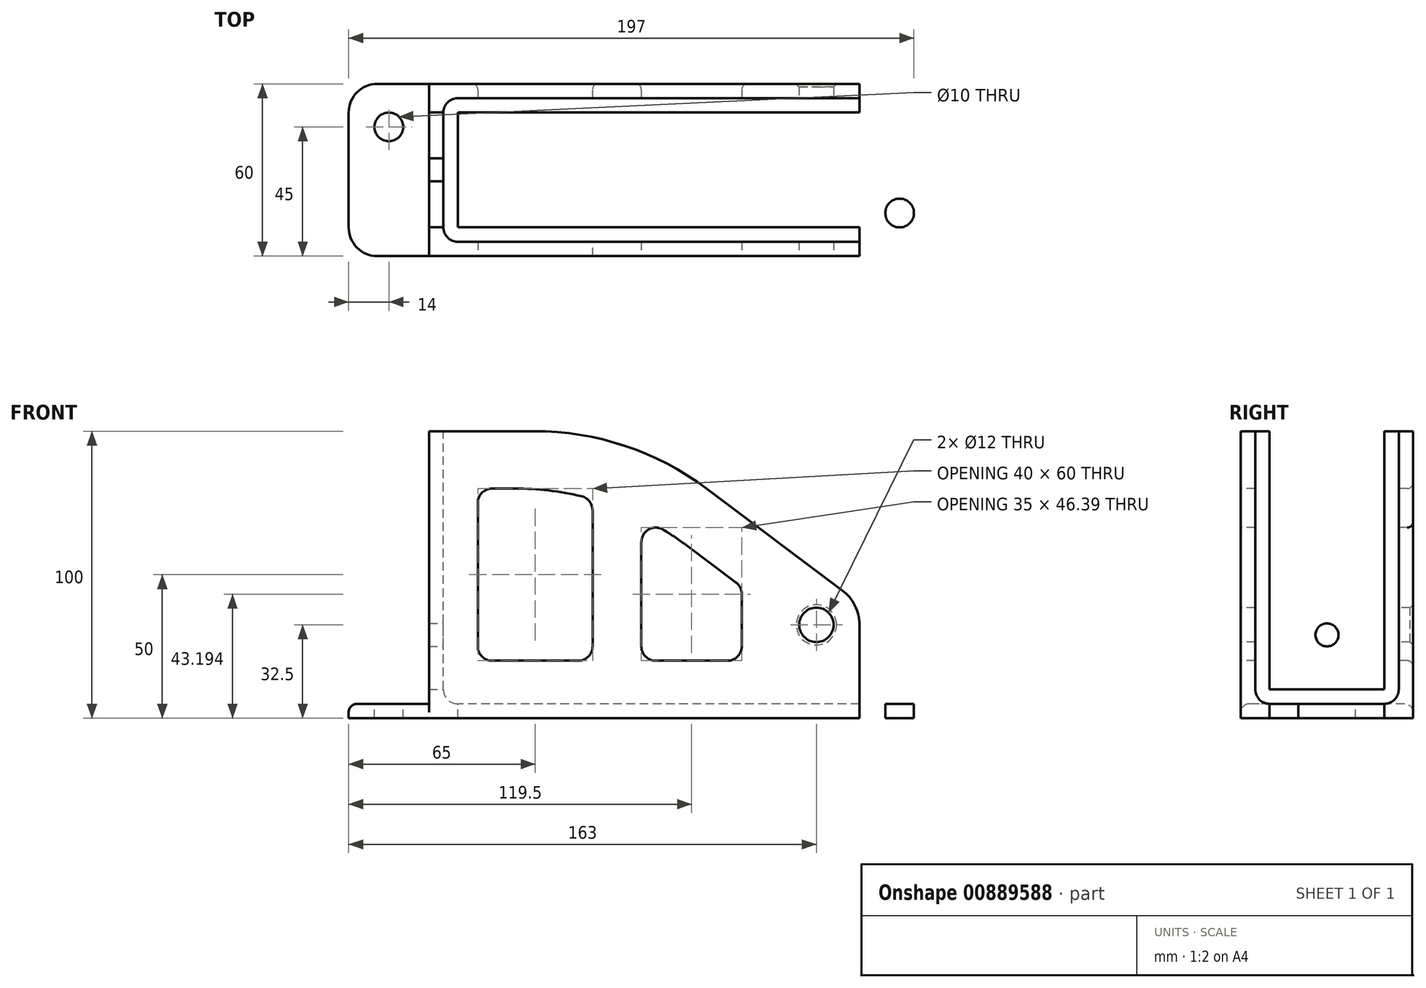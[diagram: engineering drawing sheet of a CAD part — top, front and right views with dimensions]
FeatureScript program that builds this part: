
annotation { "Feature Type Name" : "Feature", "Feature Type Description" : "" }
export const myFeature = defineFeature(function(context is Context, id is Id, definition is map)
    precondition{}
    {
        {
            var Q0;
            Q0=qCreatedBy(makeId("Front.planeOp"),FACE);
            var sketch = newSketch(context, id + "F0", { "sketchPlane" : qUnion([Q0])});
            skLineSegment(sketch, "E0", {"start": v(0, 0) * mm, "end": v(0, 100) * mm});
            skLineSegment(sketch, "E1", {"start": v(0, 100) * mm, "end": v(70, 100) * mm});
            skLineSegment(sketch, "E2", {"start": v(70, 100) * mm, "end": v(150, 40) * mm});
            skLineSegment(sketch, "E3", {"start": v(150, 40) * mm, "end": v(150, 0) * mm});
            skLineSegment(sketch, "E4", {"start": v(150, 0) * mm, "end": v(0, 0) * mm});
            skSolve(sketch);
        }
        {
            var Q0;
            Q0=makeQuery(id+"F0.imprint","IMPRINT",FACE,{"disambiguationData":[TD([[makeQuery(id+"F0.imprint","IMPRINT",EDGE,{"derivedFrom":sQuery(id+"F0.wireOp",EDGE,"E0")}),-1.0]])]});
            extrude(context, id + "F1", {"entities" : qUnion([Q0]), "depth" : 60 * mm, "offsetDistance" : 25 * mm});
        }
        {
            var Q0;
            Q0=makeQuery(id+"F1.opExtrude","SWEPT_FACE",FACE,{"disambiguationData":[OSD([sQuery(id+"F0.wireOp",EDGE,"E3")])]});
            var Q1;
            Q1=makeQuery(id+"F1.opExtrude","SWEPT_FACE",FACE,{"disambiguationData":[OSD([sQuery(id+"F0.wireOp",EDGE,"E2")])]});
            var Q2;
            Q2=makeQuery(id+"F1.opExtrude","SWEPT_FACE",FACE,{"disambiguationData":[OSD([sQuery(id+"F0.wireOp",EDGE,"E1")])]});
            shell(context, id + "F2", {"entities" : qUnion([Q0, Q1, Q2]), "thickness" : 5 * mm});
        }
        {
            var Q0;
            Q0=makeQuery(id+"F1.opExtrude","SWEPT_EDGE",EDGE,{"disambiguationData":[OSD([sQuery(id+"F0.wireOp",EDGE,"E1"),sQuery(id+"F0.wireOp",EDGE,"E2")])]});
            var Q1;
            Q1=makeQuery(id+"F2.opShell","OFFSET_EDGE",EDGE,{"disambiguationData":[OSD([sQuery(id+"F0.wireOp",EDGE,"E1"),sQuery(id+"F0.wireOp",EDGE,"E2")])]});
            fillet(context, id + "F3", {"entities" : qUnion([Q0, Q1]), "radius" : 100 * mm, "tangentPropagation" : true, "allowEdgeOverflow" : false});
        }
        {
            var Q0;
            Q0=makeQuery(id+"F1.opExtrude","SWEPT_EDGE",EDGE,{"disambiguationData":[OSD([sQuery(id+"F0.wireOp",EDGE,"E2"),sQuery(id+"F0.wireOp",EDGE,"E3")])]});
            var Q1;
            Q1=makeQuery(id+"F2.opShell","OFFSET_EDGE",EDGE,{"disambiguationData":[OSD([sQuery(id+"F0.wireOp",EDGE,"E2"),sQuery(id+"F0.wireOp",EDGE,"E3")])]});
            fillet(context, id + "F4", {"entities" : qUnion([Q0, Q1]), "radius" : 15 * mm, "tangentPropagation" : true, "allowEdgeOverflow" : false});
        }
        {
            var Q0;
            Q0=makeQuery(id+"F1.opExtrude","CAP_FACE",FACE,{"disambiguationData":[OSD([sQuery(id+"F0.wireOp",EDGE,"E0"),sQuery(id+"F0.wireOp",EDGE,"E1"),sQuery(id+"F0.wireOp",EDGE,"E2"),sQuery(id+"F0.wireOp",EDGE,"E3"),sQuery(id+"F0.wireOp",EDGE,"E4")])],"isStart":false});
            var sketch = newSketch(context, id + "F5", { "sketchPlane" : qUnion([Q0])});
            skLineSegment(sketch, "E5", {"start": v(17, 80) * mm, "end": v(30, 80) * mm});
            skLineSegment(sketch, "E6", {"start": v(90, 60) * mm, "end": v(109, 45.75) * mm});
            skLineSegment(sketch, "E7", {"start": v(109, 45.75) * mm, "end": v(109, 20) * mm});
            skLineSegment(sketch, "E8", {"start": v(109, 20) * mm, "end": v(74, 20) * mm});
            skLineSegment(sketch, "E9", {"start": v(17, 20) * mm, "end": v(17, 80) * mm});
            skPoint(sketch, "E10.visualSharp", {"position": v(63.33, 80) * mm});
            skArc(sketch, "E10.filletArc", {"start": v(90, 60) * mm, "mid": v(82.23, 65.28) * mm, "end": v(74, 69.8) * mm});
            skLineSegment(sketch, "E11", {"start": v(57, 20) * mm, "end": v(57, 76.29) * mm});
            skLineSegment(sketch, "E12", {"start": v(74, 20) * mm, "end": v(74, 69.8) * mm});
            skArc(sketch, "E13.trimOffspring", {"start": v(57, 76.29) * mm, "mid": v(43.63, 79.07) * mm, "end": v(30, 80) * mm});
            skLineSegment(sketch, "E14.trimOffspring", {"start": v(57, 20) * mm, "end": v(17, 20) * mm});
            skSolve(sketch);
        }
        {
            var Q0;
            Q0=makeQuery(id+"F5.imprint","IMPRINT",FACE,{"disambiguationData":[TD([[makeQuery(id+"F5.imprint","IMPRINT",EDGE,{"derivedFrom":sQuery(id+"F5.wireOp",EDGE,"E5")}),-1.0]])]});
            var Q1;
            Q1=makeQuery(id+"F5.imprint","IMPRINT",FACE,{"disambiguationData":[TD([[makeQuery(id+"F5.imprint","IMPRINT",EDGE,{"derivedFrom":sQuery(id+"F5.wireOp",EDGE,"E6")}),-1.0]])]});
            extrude(context, id + "F6", {"entities" : qUnion([Q0, Q1]), "operationType" : NewBodyOperationType.REMOVE, "endBound" : BoundingType.THROUGH_ALL, "oppositeDirection" : true, "depth" : 25 * mm, "offsetDistance" : 25 * mm});
        }
        {
            var Q0;
            {var subQ0=sQuery(id+"F0.wireOp",EDGE,"E4");var subQ1=sQuery(id+"F0.wireOp",EDGE,"E3");var subQ2=sQuery(id+"F0.wireOp",EDGE,"E2");var subQ3=sQuery(id+"F0.wireOp",EDGE,"E1");var subQ4=sQuery(id+"F0.wireOp",EDGE,"E0");var subQ5=makeQuery(id+"F1.opExtrude","CAP_FACE",FACE,{"disambiguationData":[OSD([subQ4,subQ3,subQ2,subQ1,subQ0])],"isStart":false});var subQ6=sQuery(id+"F5.wireOp",EDGE,"E9");var subQ7=sQuery(id+"F5.wireOp",EDGE,"E14.trimOffspring");Q0=makeQuery(id+"F6.boolean.opBoolean","COPY",EDGE,{"disambiguationData":[TD([subQ5])],"derivedFrom":makeQuery(id+"F6.opExtrude","SWEPT_EDGE",EDGE,{"disambiguationData":[OSD([subQ6,subQ7])]})});}
            var Q1;
            {var subQ0=sQuery(id+"F0.wireOp",EDGE,"E4");var subQ1=sQuery(id+"F0.wireOp",EDGE,"E3");var subQ2=sQuery(id+"F0.wireOp",EDGE,"E2");var subQ3=sQuery(id+"F0.wireOp",EDGE,"E1");var subQ4=sQuery(id+"F0.wireOp",EDGE,"E0");var subQ5=makeQuery(id+"F1.opExtrude","CAP_FACE",FACE,{"disambiguationData":[OSD([subQ4,subQ3,subQ2,subQ1,subQ0])],"isStart":false});var subQ6=sQuery(id+"F5.wireOp",EDGE,"E11");var subQ7=sQuery(id+"F5.wireOp",EDGE,"E14.trimOffspring");Q1=makeQuery(id+"F6.boolean.opBoolean","COPY",EDGE,{"disambiguationData":[TD([subQ5])],"derivedFrom":makeQuery(id+"F6.opExtrude","SWEPT_EDGE",EDGE,{"disambiguationData":[OSD([subQ6,subQ7])]})});}
            var Q2;
            {var subQ0=sQuery(id+"F0.wireOp",EDGE,"E4");var subQ1=sQuery(id+"F0.wireOp",EDGE,"E3");var subQ2=sQuery(id+"F0.wireOp",EDGE,"E2");var subQ3=sQuery(id+"F0.wireOp",EDGE,"E1");var subQ4=sQuery(id+"F0.wireOp",EDGE,"E0");var subQ5=makeQuery(id+"F1.opExtrude","CAP_FACE",FACE,{"disambiguationData":[OSD([subQ4,subQ3,subQ2,subQ1,subQ0])],"isStart":false});var subQ6=sQuery(id+"F5.wireOp",EDGE,"E12");var subQ7=sQuery(id+"F5.wireOp",EDGE,"E8");Q2=makeQuery(id+"F6.boolean.opBoolean","COPY",EDGE,{"disambiguationData":[TD([subQ5])],"derivedFrom":makeQuery(id+"F6.opExtrude","SWEPT_EDGE",EDGE,{"disambiguationData":[OSD([subQ7,subQ6])]})});}
            var Q3;
            {var subQ0=sQuery(id+"F0.wireOp",EDGE,"E4");var subQ1=sQuery(id+"F0.wireOp",EDGE,"E3");var subQ2=sQuery(id+"F0.wireOp",EDGE,"E2");var subQ3=sQuery(id+"F0.wireOp",EDGE,"E1");var subQ4=sQuery(id+"F0.wireOp",EDGE,"E0");var subQ5=makeQuery(id+"F1.opExtrude","CAP_FACE",FACE,{"disambiguationData":[OSD([subQ4,subQ3,subQ2,subQ1,subQ0])],"isStart":false});var subQ6=sQuery(id+"F5.wireOp",EDGE,"E7");var subQ7=sQuery(id+"F5.wireOp",EDGE,"E8");Q3=makeQuery(id+"F6.boolean.opBoolean","COPY",EDGE,{"disambiguationData":[TD([subQ5])],"derivedFrom":makeQuery(id+"F6.opExtrude","SWEPT_EDGE",EDGE,{"disambiguationData":[OSD([subQ6,subQ7])]})});}
            var Q4;
            {var subQ0=sQuery(id+"F0.wireOp",EDGE,"E4");var subQ1=sQuery(id+"F0.wireOp",EDGE,"E3");var subQ2=sQuery(id+"F0.wireOp",EDGE,"E2");var subQ3=sQuery(id+"F0.wireOp",EDGE,"E1");var subQ4=sQuery(id+"F0.wireOp",EDGE,"E0");var subQ5=makeQuery(id+"F1.opExtrude","CAP_FACE",FACE,{"disambiguationData":[OSD([subQ4,subQ3,subQ2,subQ1,subQ0])],"isStart":false});var subQ6=sQuery(id+"F5.wireOp",EDGE,"E5");var subQ7=sQuery(id+"F5.wireOp",EDGE,"E9");Q4=makeQuery(id+"F6.boolean.opBoolean","COPY",EDGE,{"disambiguationData":[TD([subQ5])],"derivedFrom":makeQuery(id+"F6.opExtrude","SWEPT_EDGE",EDGE,{"disambiguationData":[OSD([subQ6,subQ7])]})});}
            var Q5;
            {var subQ0=sQuery(id+"F0.wireOp",EDGE,"E4");var subQ1=sQuery(id+"F0.wireOp",EDGE,"E3");var subQ2=sQuery(id+"F0.wireOp",EDGE,"E2");var subQ3=sQuery(id+"F0.wireOp",EDGE,"E1");var subQ4=sQuery(id+"F0.wireOp",EDGE,"E0");var subQ5=makeQuery(id+"F1.opExtrude","CAP_FACE",FACE,{"disambiguationData":[OSD([subQ4,subQ3,subQ2,subQ1,subQ0])],"isStart":false});var subQ6=sQuery(id+"F5.wireOp",EDGE,"E7");var subQ7=sQuery(id+"F5.wireOp",EDGE,"E6");Q5=makeQuery(id+"F6.boolean.opBoolean","COPY",EDGE,{"disambiguationData":[TD([subQ5])],"derivedFrom":makeQuery(id+"F6.opExtrude","SWEPT_EDGE",EDGE,{"disambiguationData":[OSD([subQ7,subQ6])]})});}
            var Q6;
            {var subQ0=sQuery(id+"F0.wireOp",EDGE,"E4");var subQ1=sQuery(id+"F0.wireOp",EDGE,"E3");var subQ2=sQuery(id+"F0.wireOp",EDGE,"E2");var subQ3=sQuery(id+"F0.wireOp",EDGE,"E1");var subQ4=sQuery(id+"F0.wireOp",EDGE,"E0");var subQ5=makeQuery(id+"F1.opExtrude","CAP_FACE",FACE,{"disambiguationData":[OSD([subQ4,subQ3,subQ2,subQ1,subQ0])],"isStart":false});var subQ6=sQuery(id+"F5.wireOp",EDGE,"E13.trimOffspring");var subQ7=sQuery(id+"F5.wireOp",EDGE,"E11");Q6=makeQuery(id+"F6.boolean.opBoolean","COPY",EDGE,{"disambiguationData":[TD([subQ5])],"derivedFrom":makeQuery(id+"F6.opExtrude","SWEPT_EDGE",EDGE,{"disambiguationData":[OSD([subQ7,subQ6])]})});}
            var Q7;
            {var subQ0=sQuery(id+"F0.wireOp",EDGE,"E4");var subQ1=sQuery(id+"F0.wireOp",EDGE,"E3");var subQ2=sQuery(id+"F0.wireOp",EDGE,"E2");var subQ3=sQuery(id+"F0.wireOp",EDGE,"E1");var subQ4=sQuery(id+"F0.wireOp",EDGE,"E0");var subQ5=makeQuery(id+"F1.opExtrude","CAP_FACE",FACE,{"disambiguationData":[OSD([subQ4,subQ3,subQ2,subQ1,subQ0])],"isStart":false});var subQ6=sQuery(id+"F5.wireOp",EDGE,"E12");var subQ7=sQuery(id+"F5.wireOp",EDGE,"E10.filletArc");Q7=makeQuery(id+"F6.boolean.opBoolean","COPY",EDGE,{"disambiguationData":[TD([subQ5])],"derivedFrom":makeQuery(id+"F6.opExtrude","SWEPT_EDGE",EDGE,{"disambiguationData":[OSD([subQ7,subQ6])]})});}
            var Q8;
            {var subQ0=sQuery(id+"F0.wireOp",EDGE,"E4");var subQ1=sQuery(id+"F0.wireOp",EDGE,"E3");var subQ2=sQuery(id+"F0.wireOp",EDGE,"E2");var subQ3=sQuery(id+"F0.wireOp",EDGE,"E1");var subQ4=sQuery(id+"F0.wireOp",EDGE,"E0");var subQ5=makeQuery(id+"F1.opExtrude","CAP_FACE",FACE,{"disambiguationData":[OSD([subQ4,subQ3,subQ2,subQ1,subQ0])],"isStart":true});var subQ6=sQuery(id+"F5.wireOp",EDGE,"E7");var subQ7=sQuery(id+"F5.wireOp",EDGE,"E8");Q8=makeQuery(id+"F6.boolean.opBoolean","COPY",EDGE,{"disambiguationData":[TD([subQ5])],"derivedFrom":makeQuery(id+"F6.opExtrude","SWEPT_EDGE",EDGE,{"disambiguationData":[OSD([subQ6,subQ7])]})});}
            var Q9;
            {var subQ0=sQuery(id+"F0.wireOp",EDGE,"E4");var subQ1=sQuery(id+"F0.wireOp",EDGE,"E3");var subQ2=sQuery(id+"F0.wireOp",EDGE,"E2");var subQ3=sQuery(id+"F0.wireOp",EDGE,"E1");var subQ4=sQuery(id+"F0.wireOp",EDGE,"E0");var subQ5=makeQuery(id+"F1.opExtrude","CAP_FACE",FACE,{"disambiguationData":[OSD([subQ4,subQ3,subQ2,subQ1,subQ0])],"isStart":true});var subQ6=sQuery(id+"F5.wireOp",EDGE,"E7");var subQ7=sQuery(id+"F5.wireOp",EDGE,"E6");Q9=makeQuery(id+"F6.boolean.opBoolean","COPY",EDGE,{"disambiguationData":[TD([subQ5])],"derivedFrom":makeQuery(id+"F6.opExtrude","SWEPT_EDGE",EDGE,{"disambiguationData":[OSD([subQ7,subQ6])]})});}
            var Q10;
            {var subQ0=sQuery(id+"F0.wireOp",EDGE,"E4");var subQ1=sQuery(id+"F0.wireOp",EDGE,"E3");var subQ2=sQuery(id+"F0.wireOp",EDGE,"E2");var subQ3=sQuery(id+"F0.wireOp",EDGE,"E1");var subQ4=sQuery(id+"F0.wireOp",EDGE,"E0");var subQ5=makeQuery(id+"F1.opExtrude","CAP_FACE",FACE,{"disambiguationData":[OSD([subQ4,subQ3,subQ2,subQ1,subQ0])],"isStart":true});var subQ6=sQuery(id+"F5.wireOp",EDGE,"E12");var subQ7=sQuery(id+"F5.wireOp",EDGE,"E8");Q10=makeQuery(id+"F6.boolean.opBoolean","COPY",EDGE,{"disambiguationData":[TD([subQ5])],"derivedFrom":makeQuery(id+"F6.opExtrude","SWEPT_EDGE",EDGE,{"disambiguationData":[OSD([subQ7,subQ6])]})});}
            var Q11;
            {var subQ0=sQuery(id+"F0.wireOp",EDGE,"E4");var subQ1=sQuery(id+"F0.wireOp",EDGE,"E3");var subQ2=sQuery(id+"F0.wireOp",EDGE,"E2");var subQ3=sQuery(id+"F0.wireOp",EDGE,"E1");var subQ4=sQuery(id+"F0.wireOp",EDGE,"E0");var subQ5=makeQuery(id+"F1.opExtrude","CAP_FACE",FACE,{"disambiguationData":[OSD([subQ4,subQ3,subQ2,subQ1,subQ0])],"isStart":true});var subQ6=sQuery(id+"F5.wireOp",EDGE,"E9");var subQ7=sQuery(id+"F5.wireOp",EDGE,"E14.trimOffspring");Q11=makeQuery(id+"F6.boolean.opBoolean","COPY",EDGE,{"disambiguationData":[TD([subQ5])],"derivedFrom":makeQuery(id+"F6.opExtrude","SWEPT_EDGE",EDGE,{"disambiguationData":[OSD([subQ6,subQ7])]})});}
            var Q12;
            {var subQ0=sQuery(id+"F0.wireOp",EDGE,"E4");var subQ1=sQuery(id+"F0.wireOp",EDGE,"E3");var subQ2=sQuery(id+"F0.wireOp",EDGE,"E2");var subQ3=sQuery(id+"F0.wireOp",EDGE,"E1");var subQ4=sQuery(id+"F0.wireOp",EDGE,"E0");var subQ5=makeQuery(id+"F1.opExtrude","CAP_FACE",FACE,{"disambiguationData":[OSD([subQ4,subQ3,subQ2,subQ1,subQ0])],"isStart":true});var subQ6=sQuery(id+"F5.wireOp",EDGE,"E12");var subQ7=sQuery(id+"F5.wireOp",EDGE,"E10.filletArc");Q12=makeQuery(id+"F6.boolean.opBoolean","COPY",EDGE,{"disambiguationData":[TD([subQ5])],"derivedFrom":makeQuery(id+"F6.opExtrude","SWEPT_EDGE",EDGE,{"disambiguationData":[OSD([subQ7,subQ6])]})});}
            var Q13;
            {var subQ0=sQuery(id+"F0.wireOp",EDGE,"E4");var subQ1=sQuery(id+"F0.wireOp",EDGE,"E3");var subQ2=sQuery(id+"F0.wireOp",EDGE,"E2");var subQ3=sQuery(id+"F0.wireOp",EDGE,"E1");var subQ4=sQuery(id+"F0.wireOp",EDGE,"E0");var subQ5=makeQuery(id+"F1.opExtrude","CAP_FACE",FACE,{"disambiguationData":[OSD([subQ4,subQ3,subQ2,subQ1,subQ0])],"isStart":true});var subQ6=sQuery(id+"F5.wireOp",EDGE,"E5");var subQ7=sQuery(id+"F5.wireOp",EDGE,"E9");Q13=makeQuery(id+"F6.boolean.opBoolean","COPY",EDGE,{"disambiguationData":[TD([subQ5])],"derivedFrom":makeQuery(id+"F6.opExtrude","SWEPT_EDGE",EDGE,{"disambiguationData":[OSD([subQ6,subQ7])]})});}
            var Q14;
            {var subQ0=sQuery(id+"F0.wireOp",EDGE,"E4");var subQ1=sQuery(id+"F0.wireOp",EDGE,"E3");var subQ2=sQuery(id+"F0.wireOp",EDGE,"E2");var subQ3=sQuery(id+"F0.wireOp",EDGE,"E1");var subQ4=sQuery(id+"F0.wireOp",EDGE,"E0");var subQ5=makeQuery(id+"F1.opExtrude","CAP_FACE",FACE,{"disambiguationData":[OSD([subQ4,subQ3,subQ2,subQ1,subQ0])],"isStart":true});var subQ6=sQuery(id+"F5.wireOp",EDGE,"E11");var subQ7=sQuery(id+"F5.wireOp",EDGE,"E14.trimOffspring");Q14=makeQuery(id+"F6.boolean.opBoolean","COPY",EDGE,{"disambiguationData":[TD([subQ5])],"derivedFrom":makeQuery(id+"F6.opExtrude","SWEPT_EDGE",EDGE,{"disambiguationData":[OSD([subQ6,subQ7])]})});}
            var Q15;
            {var subQ0=sQuery(id+"F0.wireOp",EDGE,"E4");var subQ1=sQuery(id+"F0.wireOp",EDGE,"E3");var subQ2=sQuery(id+"F0.wireOp",EDGE,"E2");var subQ3=sQuery(id+"F0.wireOp",EDGE,"E1");var subQ4=sQuery(id+"F0.wireOp",EDGE,"E0");var subQ5=makeQuery(id+"F1.opExtrude","CAP_FACE",FACE,{"disambiguationData":[OSD([subQ4,subQ3,subQ2,subQ1,subQ0])],"isStart":true});var subQ6=sQuery(id+"F5.wireOp",EDGE,"E11");var subQ7=sQuery(id+"F5.wireOp",EDGE,"E13.trimOffspring");Q15=makeQuery(id+"F6.boolean.opBoolean","COPY",EDGE,{"disambiguationData":[TD([subQ5])],"derivedFrom":makeQuery(id+"F6.opExtrude","SWEPT_EDGE",EDGE,{"disambiguationData":[OSD([subQ6,subQ7])]})});}
            var Q16;
            {var subQ0=sQuery(id+"F0.wireOp",EDGE,"E4");Q16=makeQuery(id+"F2.opShell","OFFSET_EDGE",EDGE,{"disambiguationData":[OSD([subQ0]),TDD([makeQuery(id+"F1.opExtrude","CAP_EDGE",EDGE,{"disambiguationData":[OSD([subQ0])],"isStart":false})])]});}
            var Q17;
            {var subQ0=sQuery(id+"F0.wireOp",EDGE,"E4");Q17=makeQuery(id+"F2.opShell","OFFSET_EDGE",EDGE,{"disambiguationData":[OSD([subQ0]),TDD([makeQuery(id+"F1.opExtrude","CAP_EDGE",EDGE,{"disambiguationData":[OSD([subQ0])],"isStart":true})])]});}
            var Q18;
            Q18=makeQuery(id+"F2.opShell","OFFSET_EDGE",EDGE,{"disambiguationData":[OSD([sQuery(id+"F0.wireOp",EDGE,"E0"),sQuery(id+"F0.wireOp",EDGE,"E4")])]});
            var Q19;
            {var subQ0=sQuery(id+"F0.wireOp",EDGE,"E0");Q19=makeQuery(id+"F2.opShell","OFFSET_EDGE",EDGE,{"disambiguationData":[OSD([subQ0]),TDD([makeQuery(id+"F1.opExtrude","CAP_EDGE",EDGE,{"disambiguationData":[OSD([subQ0])],"isStart":false})])]});}
            var Q20;
            {var subQ0=sQuery(id+"F0.wireOp",EDGE,"E0");Q20=makeQuery(id+"F2.opShell","OFFSET_EDGE",EDGE,{"disambiguationData":[OSD([subQ0]),TDD([makeQuery(id+"F1.opExtrude","CAP_EDGE",EDGE,{"disambiguationData":[OSD([subQ0])],"isStart":true})])]});}
            fillet(context, id + "F7", {"entities" : qUnion([Q0, Q1, Q2, Q3, Q4, Q5, Q6, Q7, Q8, Q9, Q10, Q11, Q12, Q13, Q14, Q15, Q16, Q17, Q18, Q19, Q20]), "radius" : 5 * mm, "tangentPropagation" : true, "allowEdgeOverflow" : false});
        }
        {
            var Q0;
            Q0=makeQuery(id+"F1.opExtrude","SWEPT_FACE",FACE,{"disambiguationData":[OSD([sQuery(id+"F0.wireOp",EDGE,"E3")])]});
            var sketch = newSketch(context, id + "F8", { "sketchPlane" : qUnion([Q0])});
            skLineSegment(sketch, "E15.bottom", {"start": v(-60, 0) * mm, "end": v(0, 0) * mm});
            skLineSegment(sketch, "E15.top", {"start": v(-60, 5) * mm, "end": v(0, 5) * mm});
            skLineSegment(sketch, "E15.left", {"start": v(-60, 0) * mm, "end": v(-60, 5) * mm});
            skLineSegment(sketch, "E15.right", {"start": v(0, 0) * mm, "end": v(0, 5) * mm});
            skSolve(sketch);
        }
        {
            var Q0;
            Q0=makeQuery(id+"F8.imprint","IMPRINT",FACE,{"disambiguationData":[TD([[makeQuery(id+"F8.imprint","IMPRINT",EDGE,{"derivedFrom":sQuery(id+"F8.wireOp",EDGE,"E15.bottom")}),1.0]])]});
            extrude(context, id + "F9", {"entities" : qUnion([Q0]), "operationType" : NewBodyOperationType.ADD, "depth" : 28 * mm, "offsetDistance" : 25 * mm});
        }
        {
            var Q0;
            Q0=makeQuery(id+"F1.opExtrude","SWEPT_FACE",FACE,{"disambiguationData":[OSD([sQuery(id+"F0.wireOp",EDGE,"E0")])]});
            var sketch = newSketch(context, id + "F10", { "sketchPlane" : qUnion([Q0])});
            skLineSegment(sketch, "E16.bottom", {"start": v(0, 0) * mm, "end": v(60, 0) * mm});
            skLineSegment(sketch, "E16.top", {"start": v(0, 5) * mm, "end": v(60, 5) * mm});
            skLineSegment(sketch, "E16.left", {"start": v(0, 0) * mm, "end": v(0, 5) * mm});
            skLineSegment(sketch, "E16.right", {"start": v(60, 0) * mm, "end": v(60, 5) * mm});
            skSolve(sketch);
        }
        {
            var Q0;
            Q0=makeQuery(id+"F10.imprint","IMPRINT",FACE,{"disambiguationData":[TD([[makeQuery(id+"F10.imprint","IMPRINT",EDGE,{"derivedFrom":sQuery(id+"F10.wireOp",EDGE,"E16.bottom")}),-1.0]])]});
            extrude(context, id + "F11", {"entities" : qUnion([Q0]), "operationType" : NewBodyOperationType.ADD, "depth" : 28 * mm, "offsetDistance" : 25 * mm});
        }
        {
            var Q0;
            Q0=makeQuery(id+"F11.opExtrude","CAP_EDGE",EDGE,{"disambiguationData":[OSD([sQuery(id+"F10.wireOp",EDGE,"E16.right")])],"isStart":false});
            var Q1;
            Q1=makeQuery(id+"F9.opExtrude","CAP_EDGE",EDGE,{"disambiguationData":[OSD([sQuery(id+"F8.wireOp",EDGE,"E15.left")])],"isStart":false});
            var Q2;
            Q2=makeQuery(id+"F9.opExtrude","CAP_EDGE",EDGE,{"disambiguationData":[OSD([sQuery(id+"F8.wireOp",EDGE,"E15.right")])],"isStart":false});
            var Q3;
            Q3=makeQuery(id+"F11.opExtrude","CAP_EDGE",EDGE,{"disambiguationData":[OSD([sQuery(id+"F10.wireOp",EDGE,"E16.left")])],"isStart":false});
            fillet(context, id + "F12", {"entities" : qUnion([Q0, Q1, Q2, Q3]), "radius" : 10 * mm, "tangentPropagation" : true, "allowEdgeOverflow" : false});
        }
        {
            var Q0;
            Q0=makeQuery(id+"F9.boolean.opBoolean","MERGE",FACE,{"derivedFrom":[makeQuery(id+"F2.opShell","OFFSET_FACE",FACE,{"disambiguationData":[OSD([sQuery(id+"F0.wireOp",EDGE,"E4")])]}),makeQuery(id+"F9.opExtrude","SWEPT_FACE",FACE,{"disambiguationData":[OSD([sQuery(id+"F8.wireOp",EDGE,"E15.top")])]})]});
            var sketch = newSketch(context, id + "F13", { "sketchPlane" : qUnion([Q0])});
            skLineSegment(sketch, "E17", {"start": v(-47.2, -30) * mm, "end": v(216.18, -30) * mm, "construction": true});
            skCircle(sketch, "E18", {"center": v(164, -15) * mm, "radius": 5 * mm});
            skCircle(sketch, "E19.MirrorC", {"center": v(164, -45) * mm, "radius": 5 * mm});
            skCircle(sketch, "E20", {"center": v(-14, -15) * mm, "radius": 5 * mm});
            skCircle(sketch, "E21.MirrorC", {"center": v(-14, -45) * mm, "radius": 5 * mm});
            skSolve(sketch);
        }
        {
            var Q0;
            Q0=makeQuery(id+"F13.imprint","IMPRINT",FACE,{"disambiguationData":[TD([[makeQuery(id+"F13.imprint","IMPRINT",EDGE,{"derivedFrom":sQuery(id+"F13.wireOp",EDGE,"E21.MirrorC")}),-1.0]])]});
            var Q1;
            Q1=makeQuery(id+"F13.imprint","IMPRINT",FACE,{"disambiguationData":[TD([[makeQuery(id+"F13.imprint","IMPRINT",EDGE,{"derivedFrom":sQuery(id+"F13.wireOp",EDGE,"E20")}),1.0]])]});
            var Q2;
            Q2=makeQuery(id+"F13.imprint","IMPRINT",FACE,{"disambiguationData":[TD([[makeQuery(id+"F13.imprint","IMPRINT",EDGE,{"derivedFrom":sQuery(id+"F13.wireOp",EDGE,"E19.MirrorC")}),-1.0]])]});
            var Q3;
            Q3=makeQuery(id+"F13.imprint","IMPRINT",FACE,{"disambiguationData":[TD([[makeQuery(id+"F13.imprint","IMPRINT",EDGE,{"derivedFrom":sQuery(id+"F13.wireOp",EDGE,"E18")}),1.0]])]});
            extrude(context, id + "F14", {"entities" : qUnion([Q0, Q1, Q2, Q3]), "operationType" : NewBodyOperationType.REMOVE, "oppositeDirection" : true, "depth" : 25 * mm, "offsetDistance" : 25 * mm});
        }
        {
            var Q0;
            Q0=makeQuery(id+"F11.opExtrude","CAP_EDGE",EDGE,{"disambiguationData":[OSD([sQuery(id+"F10.wireOp",EDGE,"E16.top")])],"isStart":true});
            var Q1;
            Q1=makeQuery(id+"F12.opFillet","BLEND_EDGE",EDGE,{"blendedFrom":[makeQuery(id+"F11.opExtrude","CAP_EDGE",EDGE,{"disambiguationData":[OSD([sQuery(id+"F10.wireOp",EDGE,"E16.right")])],"isStart":false}),makeQuery(id+"F11.opExtrude","SWEPT_FACE",FACE,{"disambiguationData":[OSD([sQuery(id+"F10.wireOp",EDGE,"E16.top")])]})],"blendedInto":[makeQuery(id+"F11.opExtrude","SWEPT_FACE",FACE,{"disambiguationData":[OSD([sQuery(id+"F10.wireOp",EDGE,"E16.top")])]})]});
            var Q2;
            {var subQ2=sQuery(id+"F8.wireOp",EDGE,"E15.top");Q2=makeQuery(id+"F9.boolean.opBoolean","SPLIT",EDGE,{"disambiguationData":[TD([makeQuery(id+"F9.opExtrude","SWEPT_FACE",FACE,{"disambiguationData":[OSD([sQuery(id+"F8.wireOp",EDGE,"E15.left")])]})])],"derivedFrom":makeQuery(id+"F9.opExtrude","CAP_EDGE",EDGE,{"disambiguationData":[OSD([subQ2])],"isStart":true})});}
            var Q3;
            {var subQ2=sQuery(id+"F8.wireOp",EDGE,"E15.top");Q3=makeQuery(id+"F9.boolean.opBoolean","SPLIT",EDGE,{"disambiguationData":[TD([makeQuery(id+"F9.opExtrude","SWEPT_FACE",FACE,{"disambiguationData":[OSD([sQuery(id+"F8.wireOp",EDGE,"E15.right")])]})])],"derivedFrom":makeQuery(id+"F9.opExtrude","CAP_EDGE",EDGE,{"disambiguationData":[OSD([subQ2])],"isStart":true})});}
            var Q4;
            Q4=makeQuery(id+"F9.opExtrude","CAP_EDGE",EDGE,{"disambiguationData":[OSD([sQuery(id+"F8.wireOp",EDGE,"E15.top")])],"isStart":false});
            fillet(context, id + "F15", {"entities" : qUnion([Q0, Q1, Q2, Q3, Q4]), "radius" : 3 * mm, "tangentPropagation" : true, "allowEdgeOverflow" : false});
        }
        {
            var Q0;
            Q0=makeQuery(id+"F6.boolean.opBoolean","INTERSECT",EDGE,{"derivedFrom":[makeQuery(id+"F1.opExtrude","CAP_FACE",FACE,{"disambiguationData":[OSD([sQuery(id+"F0.wireOp",EDGE,"E0"),sQuery(id+"F0.wireOp",EDGE,"E1"),sQuery(id+"F0.wireOp",EDGE,"E2"),sQuery(id+"F0.wireOp",EDGE,"E3"),sQuery(id+"F0.wireOp",EDGE,"E4")])],"isStart":true}),makeQuery(id+"F6.opExtrude","SWEPT_FACE",FACE,{"disambiguationData":[OSD([sQuery(id+"F5.wireOp",EDGE,"E8")])]})]});
            var Q1;
            Q1=makeQuery(id+"F6.boolean.opBoolean","INTERSECT",EDGE,{"derivedFrom":[makeQuery(id+"F1.opExtrude","CAP_FACE",FACE,{"disambiguationData":[OSD([sQuery(id+"F0.wireOp",EDGE,"E0"),sQuery(id+"F0.wireOp",EDGE,"E1"),sQuery(id+"F0.wireOp",EDGE,"E2"),sQuery(id+"F0.wireOp",EDGE,"E3"),sQuery(id+"F0.wireOp",EDGE,"E4")])],"isStart":true}),makeQuery(id+"F6.opExtrude","SWEPT_FACE",FACE,{"disambiguationData":[OSD([sQuery(id+"F5.wireOp",EDGE,"E14.trimOffspring")])]})]});
            var Q2;
            Q2=makeQuery(id+"F6.boolean.opBoolean","COPY",EDGE,{"derivedFrom":makeQuery(id+"F6.opExtrude","CAP_EDGE",EDGE,{"disambiguationData":[OSD([sQuery(id+"F5.wireOp",EDGE,"E8")])],"isStart":true})});
            var Q3;
            Q3=makeQuery(id+"F6.boolean.opBoolean","COPY",EDGE,{"derivedFrom":makeQuery(id+"F6.opExtrude","CAP_EDGE",EDGE,{"disambiguationData":[OSD([sQuery(id+"F5.wireOp",EDGE,"E14.trimOffspring")])],"isStart":true})});
            fillet(context, id + "F16", {"entities" : qUnion([Q0, Q1, Q2, Q3]), "radius" : 2 * mm, "tangentPropagation" : true, "allowEdgeOverflow" : false});
        }
        {
            var Q0;
            Q0=makeQuery(id+"F11.boolean.opBoolean","MERGE",FACE,{"derivedFrom":[makeQuery(id+"F9.boolean.opBoolean","MERGE",FACE,{"derivedFrom":[makeQuery(id+"F1.opExtrude","CAP_FACE",FACE,{"disambiguationData":[OSD([sQuery(id+"F0.wireOp",EDGE,"E0"),sQuery(id+"F0.wireOp",EDGE,"E1"),sQuery(id+"F0.wireOp",EDGE,"E2"),sQuery(id+"F0.wireOp",EDGE,"E3"),sQuery(id+"F0.wireOp",EDGE,"E4")])],"isStart":false}),makeQuery(id+"F9.opExtrude","SWEPT_FACE",FACE,{"disambiguationData":[OSD([sQuery(id+"F8.wireOp",EDGE,"E15.left")])]})]}),makeQuery(id+"F11.opExtrude","SWEPT_FACE",FACE,{"disambiguationData":[OSD([sQuery(id+"F10.wireOp",EDGE,"E16.right")])]})]});
            var sketch = newSketch(context, id + "F17", { "sketchPlane" : qUnion([Q0])});
            skCircle(sketch, "E22", {"center": v(135, 32.5) * mm, "radius": 6 * mm});
            skSolve(sketch);
        }
        {
            var Q0;
            Q0=makeQuery(id+"F17.imprint","IMPRINT",FACE,{"disambiguationData":[TD([[makeQuery(id+"F17.imprint","IMPRINT",EDGE,{"derivedFrom":sQuery(id+"F17.wireOp",EDGE,"E22")}),1.0]])]});
            extrude(context, id + "F18", {"entities" : qUnion([Q0]), "operationType" : NewBodyOperationType.REMOVE, "endBound" : BoundingType.THROUGH_ALL, "oppositeDirection" : true, "depth" : 25 * mm, "offsetDistance" : 25 * mm});
        }
        {
            var Q0;
            Q0=makeQuery(id+"F14.boolean.opBoolean","COPY",EDGE,{"derivedFrom":makeQuery(id+"F14.opExtrude","CAP_EDGE",EDGE,{"disambiguationData":[OSD([sQuery(id+"F13.wireOp",EDGE,"E21.MirrorC")])],"isStart":true})});
            var Q1;
            Q1=makeQuery(id+"F14.boolean.opBoolean","COPY",EDGE,{"derivedFrom":makeQuery(id+"F14.opExtrude","CAP_EDGE",EDGE,{"disambiguationData":[OSD([sQuery(id+"F13.wireOp",EDGE,"E20")])],"isStart":true})});
            var Q2;
            Q2=makeQuery(id+"F14.boolean.opBoolean","COPY",EDGE,{"derivedFrom":makeQuery(id+"F14.opExtrude","CAP_EDGE",EDGE,{"disambiguationData":[OSD([sQuery(id+"F13.wireOp",EDGE,"E18")])],"isStart":true})});
            var Q3;
            Q3=makeQuery(id+"F14.boolean.opBoolean","COPY",EDGE,{"derivedFrom":makeQuery(id+"F14.opExtrude","CAP_EDGE",EDGE,{"disambiguationData":[OSD([sQuery(id+"F13.wireOp",EDGE,"E19.MirrorC")])],"isStart":true})});
            var Q4;
            Q4=makeQuery(id+"F18.boolean.opBoolean","COPY",EDGE,{"derivedFrom":makeQuery(id+"F18.opExtrude","CAP_EDGE",EDGE,{"disambiguationData":[OSD([sQuery(id+"F17.wireOp",EDGE,"E22")])],"isStart":true})});
            var Q5;
            Q5=makeQuery(id+"F18.boolean.opBoolean","INTERSECT",EDGE,{"derivedFrom":[makeQuery(id+"F11.boolean.opBoolean","MERGE",FACE,{"derivedFrom":[makeQuery(id+"F9.boolean.opBoolean","MERGE",FACE,{"derivedFrom":[makeQuery(id+"F1.opExtrude","CAP_FACE",FACE,{"disambiguationData":[OSD([sQuery(id+"F0.wireOp",EDGE,"E0"),sQuery(id+"F0.wireOp",EDGE,"E1"),sQuery(id+"F0.wireOp",EDGE,"E2"),sQuery(id+"F0.wireOp",EDGE,"E3"),sQuery(id+"F0.wireOp",EDGE,"E4")])],"isStart":true}),makeQuery(id+"F9.opExtrude","SWEPT_FACE",FACE,{"disambiguationData":[OSD([sQuery(id+"F8.wireOp",EDGE,"E15.right")])]})]}),makeQuery(id+"F11.opExtrude","SWEPT_FACE",FACE,{"disambiguationData":[OSD([sQuery(id+"F10.wireOp",EDGE,"E16.left")])]})]}),makeQuery(id+"F18.opExtrude","SWEPT_FACE",FACE,{"disambiguationData":[OSD([sQuery(id+"F17.wireOp",EDGE,"E22")])]})]});
            chamfer(context, id + "F19", {"entities" : qUnion([Q0, Q1, Q2, Q3, Q4, Q5]), "width" : 1 * mm, "tangentPropagation" : true});
        }
        {
            var Q0;
            Q0=makeQuery(id+"F2.opShell","OFFSET_FACE",FACE,{"disambiguationData":[OSD([sQuery(id+"F0.wireOp",EDGE,"E0")])]});
            var sketch = newSketch(context, id + "F20", { "sketchPlane" : qUnion([Q0])});
            skCircle(sketch, "E23", {"center": v(-30, 55) * mm, "radius": 15 * mm});
            skLineSegment(sketch, "E24", {"start": v(-30, 99.65) * mm, "end": v(-30, -25.87) * mm, "construction": true});
            skLineSegment(sketch, "E25", {"start": v(-101.8, 55) * mm, "end": v(95.94, 55) * mm, "construction": true});
            skCircle(sketch, "E26", {"center": v(-30, 81) * mm, "radius": 4 * mm});
            skCircle(sketch, "E27.MirrorC", {"center": v(-30, 29) * mm, "radius": 4 * mm});
            skSolve(sketch);
        }
        {
            var Q0;
            Q0=makeQuery(id+"F20.imprint","IMPRINT",FACE,{"disambiguationData":[TD([[makeQuery(id+"F20.imprint","IMPRINT",EDGE,{"derivedFrom":sQuery(id+"F20.wireOp",EDGE,"E27.MirrorC")}),-1.0]])]});
            var Q1;
            Q1=makeQuery(id+"F20.imprint","IMPRINT",FACE,{"disambiguationData":[TD([[makeQuery(id+"F20.imprint","IMPRINT",EDGE,{"derivedFrom":sQuery(id+"F20.wireOp",EDGE,"E23")}),1.0]])]});
            var Q2;
            Q2=makeQuery(id+"F20.imprint","IMPRINT",FACE,{"disambiguationData":[TD([[makeQuery(id+"F20.imprint","IMPRINT",EDGE,{"derivedFrom":sQuery(id+"F20.wireOp",EDGE,"E26")}),1.0]])]});
            extrude(context, id + "F21", {"entities" : qUnion([Q0, Q1, Q2]), "operationType" : NewBodyOperationType.REMOVE, "oppositeDirection" : true, "depth" : 25 * mm, "offsetDistance" : 25 * mm});
        }
    });
